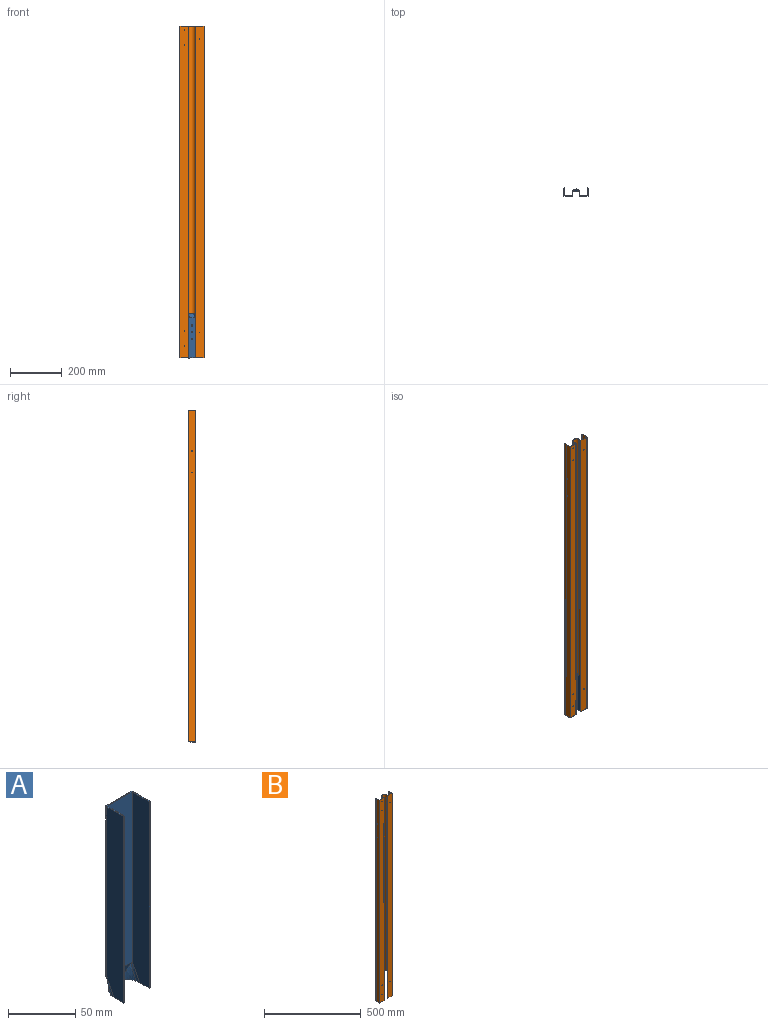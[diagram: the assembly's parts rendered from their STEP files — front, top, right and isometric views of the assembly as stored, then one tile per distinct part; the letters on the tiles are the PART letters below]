
ASSEMBLY  parts=2 mates=1
PART A: 27 faces, bbox 35.2x31.2x177.2 mm
  f0: cylinder r=2.75mm len=5.5mm, axis (0,1,0), area 17.3mm2, adj f5,f17
  f1: cylinder r=2.75mm len=5.5mm, axis (0,1,0), area 17.3mm2, adj f5,f17
  f2: cylinder r=2.75mm len=5.5mm, axis (0,1,0), area 17.3mm2, adj f5,f17
  f3: cylinder r=2mm len=155mm, axis (0,0,1), area 76mm2, adj f5,f7,f12,f13
  f4: cylinder r=2mm len=155mm, axis (0,0,1), area 76mm2, adj f5,f10,f11,f13
  f5: plane 155.16x25.88mm, normal (0,-1,0), area 3944.4mm2, adj f0,f1,f2,f3,f4,f6,f7,f11
  f6: plane 31.84x20.86mm, normal (0,-0.95,-0.32), area 252.1mm2, adj f5,f7,f8,f9,f11,f22
  f7: bspline ~15.36x9.22mm, area 39.2mm2, adj f3,f5,f6,f8,f12,f22
  f8: bspline ~13.47x11.57mm, area 74.8mm2, adj f6,f7,f22
  f9: bspline ~13.47x11.57mm, area 74.8mm2, adj f6,f11,f22
  f10: plane 170x17.51mm, normal (1,0,0), area 2921.1mm2, adj f4,f11,f13,f22,f23
  f11: bspline ~15.36x9.22mm, area 39.2mm2, adj f4,f5,f6,f9,f10,f22
  f12: plane 170x17.51mm, normal (-1,0,0), area 2921.1mm2, adj f3,f7,f13,f14,f22
  f13: plane 28x19mm, normal (0,0,1), area 63.6mm2, adj f3,f4,f5,f10,f12,f14,f15,f16
  f14: plane 170x1mm, normal (0,-1,0), area 170mm2, adj f12,f13,f22,f26
  f15: cylinder r=3mm len=155mm, axis (0,0,1), area 240.9mm2, adj f13,f17,f19,f26
  f16: cylinder r=3mm len=155mm, axis (0,0,1), area 240.9mm2, adj f13,f17,f24,f25
  f17: plane 155x27.21mm, normal (0,1,0), area 4146.7mm2, adj f0,f1,f2,f13,f15,f16,f18
  f18: plane 34.37x22.16mm, normal (0,0.95,0.32), area 265.2mm2, adj f17,f19,f20,f21,f25
  f19: bspline ~15x9.97mm, area 49.2mm2, adj f15,f18,f20,f22,f26
  f20: bspline ~13.73x13.57mm, area 89.1mm2, adj f18,f19,f22
  f21: bspline ~13.7x13.48mm, area 89.1mm2, adj f18,f22,f25
  f22: plane 34.23x30.23mm, normal (0,0,-1), area 62.5mm2, adj f6,f7,f8,f9,f10,f11,f12,f14
  f23: plane 170x1mm, normal (0,-1,0), area 170mm2, adj f10,f13,f22,f24
  f24: plane 170x17.51mm, normal (-1,0,0), area 2921.1mm2, adj f13,f16,f22,f23,f25
  f25: bspline ~15x9.97mm, area 49.2mm2, adj f16,f18,f21,f22,f24
  f26: plane 170x17.51mm, normal (1,0,0), area 2921.1mm2, adj f13,f14,f15,f19,f22
PART B: 38 faces, bbox 93x29x1282 mm
  f0: cylinder r=13mm len=1112mm, axis (0,0,-1), area 45414.9mm2, adj f12,f13,f26,f37
  f1: plane 1112x10mm, normal (1,0,0), area 11120mm2, adj f2,f22,f26,f37
  f2: cylinder r=14mm len=1112mm, axis (0,0,-1), area 48908.3mm2, adj f1,f3,f26,f37
  f3: plane 1112x10mm, normal (-1,0,0), area 11120mm2, adj f2,f23,f26,f37
  f4: plane 33.5x29mm, normal (0,0,-1), area 68.6mm2, adj f13,f14,f15,f16,f17,f18,f19,f20
  f5: plane 33.5x29mm, normal (0,0,-1), area 68.6mm2, adj f6,f7,f8,f9,f10,f11,f12,f23
  f6: plane 1282x5.25mm, normal (-0.99,0.17,0), area 6825.2mm2, adj f5,f7,f25,f26
  f7: plane 1282x0.99mm, normal (-0.17,-0.99,0), area 1282mm2, adj f5,f6,f8,f26
  f8: plane 1282x5.25mm, normal (0.99,-0.17,0), area 6825.2mm2, adj f5,f7,f9,f26
  f9: cylinder r=1.5mm len=1282mm, axis (0,0,-1), area 6365.3mm2, adj f5,f8,f10,f26
  f10: plane 1282x27.5mm, normal (-1,0,0), area 35240.9mm2, adj f5,f9,f11,f26,f30,f31
  f11: plane 1282x33.5mm, normal (0,-1,0), area 42918.7mm2, adj f5,f10,f12,f26,f27,f28,f34,f35
  f12: plane 1282x11mm, normal (1,0,0), area 12402mm2, adj f0,f5,f11,f23,f26,f37
  f13: plane 1282x11mm, normal (-1,0,0), area 12402mm2, adj f0,f4,f14,f22,f26,f37
  f14: plane 1282x33.5mm, normal (0,-1,0), area 42932.9mm2, adj f4,f13,f15,f26,f29,f36
  f15: plane 1282x27.5mm, normal (1,0,0), area 35240.9mm2, adj f4,f14,f16,f26,f32,f33
  f16: cylinder r=1.5mm len=1282mm, axis (0,0,-1), area 6365.3mm2, adj f4,f15,f17,f26
  f17: plane 1282x5.25mm, normal (-0.99,-0.17,0), area 6825.2mm2, adj f4,f16,f18,f26
  f18: plane 1282x0.99mm, normal (0.17,-0.99,0), area 1282mm2, adj f4,f17,f19,f26
  f19: plane 1282x5.25mm, normal (0.99,0.17,0), area 6825.2mm2, adj f4,f18,f20,f26
  f20: cylinder r=0.5mm len=1282mm, axis (0,0,-1), area 2121.8mm2, adj f4,f19,f21,f26
  f21: plane 1282x26.5mm, normal (-1,0,0), area 33958.9mm2, adj f4,f20,f22,f26,f32,f33
  f22: plane 1282x32.5mm, normal (0,1,0), area 40538.9mm2, adj f1,f4,f13,f21,f26,f29,f36,f37
  f23: plane 1282x32.5mm, normal (0,1,0), area 40524.7mm2, adj f3,f5,f12,f24,f26,f27,f28,f34
  f24: plane 1282x26.5mm, normal (1,0,0), area 33958.9mm2, adj f5,f23,f25,f26,f30,f31
  f25: cylinder r=0.5mm len=1282mm, axis (0,0,-1), area 2121.8mm2, adj f5,f6,f24,f26
  f26: plane 93x29mm, normal (0,0,1), area 199.7mm2, adj f0,f1,f2,f3,f6,f7,f8,f9
  f27: cylinder r=1.5mm len=3mm, axis (0,-1,0), area 9.4mm2, adj f11,f23
  f28: cylinder r=1.5mm len=3mm, axis (0,-1,0), area 9.4mm2, adj f11,f23
  f29: cylinder r=1.5mm len=3mm, axis (0,-1,0), area 9.4mm2, adj f14,f22
  f30: cylinder r=1.5mm len=3mm, axis (1,0,0), area 9.4mm2, adj f10,f24
  f31: cylinder r=1.5mm len=3mm, axis (1,0,0), area 9.4mm2, adj f10,f24
  f32: cylinder r=1.5mm len=3mm, axis (1,0,0), area 9.4mm2, adj f15,f21
  f33: cylinder r=1.5mm len=3mm, axis (1,0,0), area 9.4mm2, adj f15,f21
  f34: cylinder r=1.5mm len=3mm, axis (0,-1,0), area 9.4mm2, adj f11,f23
  f35: cylinder r=1.5mm len=3mm, axis (0,-1,0), area 9.4mm2, adj f11,f23
  f36: cylinder r=1.5mm len=3mm, axis (0,-1,0), area 9.4mm2, adj f14,f22
  f37: plane 28x24mm, normal (0,0,-1), area 62.4mm2, adj f0,f1,f2,f3,f12,f13,f22,f23
PLACE A rot(axis=(0,1,0),180deg) t=(1148.98,-429.78,-621.81)mm
PLACE B t=(-1.02,0.22,-791.81)mm fixed
MATE fastened A.f22 <-> B.f37  axis (0,0,1) through (1162.98,-439.78,-621.81)mm
